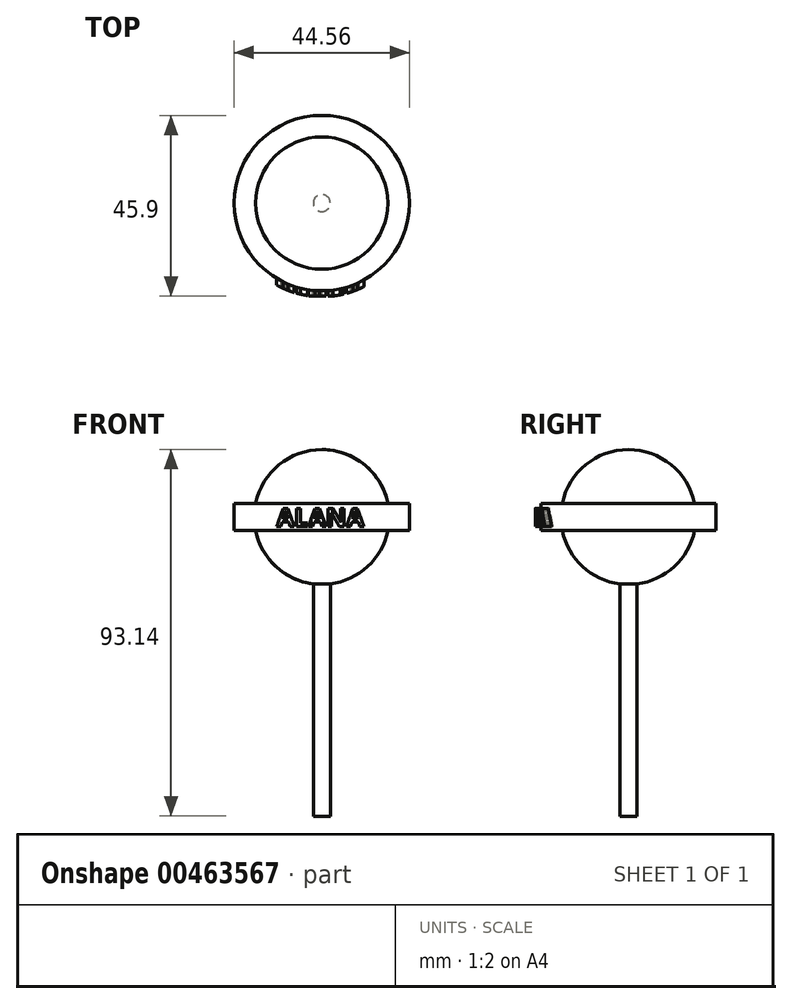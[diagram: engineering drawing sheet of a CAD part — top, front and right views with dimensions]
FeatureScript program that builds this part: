
annotation { "Feature Type Name" : "Feature", "Feature Type Description" : "" }
export const myFeature = defineFeature(function(context is Context, id is Id, definition is map)
    precondition{}
    {
        {
            var Q0;
            Q0=qCreatedBy(makeId("Front.planeOp"),FACE);
            var sketch = newSketch(context, id + "F0", { "sketchPlane" : qUnion([Q0])});
            skArc(sketch, "E0", {"start": v(0, -17.15) * mm, "mid": v(17.15, 0) * mm, "end": v(0, 17.15) * mm});
            skLineSegment(sketch, "E1", {"start": v(0, 17.15) * mm, "end": v(0, -17.15) * mm});
            skLineSegment(sketch, "E2", {"start": v(0, 0) * mm, "end": v(0, 50.78) * mm, "construction": true});
            skLineSegment(sketch, "E3.bottom", {"start": v(22.28, 3.47) * mm, "end": v(2.16, 3.47) * mm});
            skLineSegment(sketch, "E3.top", {"start": v(22.28, -3.47) * mm, "end": v(2.16, -3.47) * mm});
            skLineSegment(sketch, "E3.left", {"start": v(22.28, 3.47) * mm, "end": v(22.28, -3.47) * mm});
            skLineSegment(sketch, "E3.right", {"start": v(2.16, 3.47) * mm, "end": v(2.16, -3.47) * mm});
            skPoint(sketch, "E3.middle", {"position": v(12.22, 0) * mm});
            skLineSegment(sketch, "E4.bottom", {"start": v(0, -13.6) * mm, "end": v(2.16, -13.6) * mm});
            skLineSegment(sketch, "E4.top", {"start": v(0, -76) * mm, "end": v(2.16, -76) * mm});
            skLineSegment(sketch, "E4.left", {"start": v(0, -13.6) * mm, "end": v(0, -76) * mm});
            skLineSegment(sketch, "E4.right", {"start": v(2.16, -13.6) * mm, "end": v(2.16, -76) * mm});
            skLineSegment(sketch, "E5", {"start": v(0, 0) * mm, "end": v(0, 35.7) * mm, "construction": true});
            skSolve(sketch);
        }
        {
            var Q0;
            Q0 = qSketchRegion(id + "F0", true);
            var Q1;
            Q1=sQuery(id+"F0.wireOp",EDGE,"E2");
            revolve(context, id + "F1", {"entities" : qUnion([Q0]), "axis" : qUnion([Q1]), "revolveType" : RevolveType.FULL});
        }
        {
            var Q0;
            Q0=qCreatedBy(makeId("Front.planeOp"),FACE);
            var sketch = newSketch(context, id + "F2", { "sketchPlane" : qUnion([Q0])});
            skText(sketch, "E6", { "text": "ALANA", "fontName": "OpenSans-Bold.ttf"});
            const initialGuessF2  = {"E6": [-0.01144, -0.00237, 1, 0, 0.00462]};
            skSetInitialGuess(sketch, initialGuessF2);
            skSolve(sketch);
        }
        {
            var Q0;
            Q0 = qSketchRegion(id + "F2", true);
            extrude(context, id + "F3", {"entities" : qUnion([Q0]), "operationType" : NewBodyOperationType.ADD, "depth" : 23.62 * mm});
        }
        {
            var Q0;
            Q0=qCreatedBy(makeId("Front.planeOp"),FACE);
            var sketch = newSketch(context, id + "F4", { "sketchPlane" : qUnion([Q0])});
            skLineSegment(sketch, "E7", {"start": v(22.28, 3.47) * mm, "end": v(22.28, -3.47) * mm});
            skLineSegment(sketch, "E8.0", {"start": v(23.78, -4.97) * mm, "end": v(17.32, -4.97) * mm});
            skLineSegment(sketch, "E8.1", {"start": v(23.78, 4.97) * mm, "end": v(23.78, -4.97) * mm});
            skLineSegment(sketch, "E8.2", {"start": v(23.78, 4.97) * mm, "end": v(16.8, 4.97) * mm});
            skLineSegment(sketch, "E9", {"start": v(16.8, 4.97) * mm, "end": v(14.12, 13.06) * mm});
            skLineSegment(sketch, "E10", {"start": v(14.12, 13.06) * mm, "end": v(25.18, 24.98) * mm});
            skLineSegment(sketch, "E11", {"start": v(25.18, 24.98) * mm, "end": v(38.63, 7.96) * mm});
            skLineSegment(sketch, "E12", {"start": v(38.63, 7.96) * mm, "end": v(38.63, -8.9) * mm});
            skLineSegment(sketch, "E13", {"start": v(38.63, -8.9) * mm, "end": v(32, -11.32) * mm});
            skLineSegment(sketch, "E14", {"start": v(32, -11.32) * mm, "end": v(23.99, -13.54) * mm});
            skLineSegment(sketch, "E15", {"start": v(23.99, -13.54) * mm, "end": v(17.32, -4.97) * mm});
            skLineSegment(sketch, "E16", {"start": v(0, 0) * mm, "end": v(0, 36.04) * mm, "construction": true});
            skSolve(sketch);
        }
        {
            var Q0;
            Q0 = qSketchRegion(id + "F4", true);
            var Q1;
            Q1=sQuery(id+"F4.wireOp",EDGE,"E16");
            revolve(context, id + "F5", {"operationType" : NewBodyOperationType.REMOVE, "entities" : qUnion([Q0]), "axis" : qUnion([Q1]), "revolveType" : RevolveType.FULL, "oppositeDirection" : true});
        }
    });
